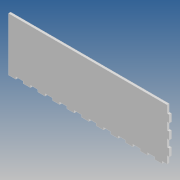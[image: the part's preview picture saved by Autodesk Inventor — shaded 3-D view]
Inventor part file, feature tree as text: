
AUTODESK INVENTOR PART (.ipt)
format: ipt  version: 2020 (Build 240168000, 168)  size: 154,112 bytes
history: native  units: mm
features: extrude x3, sketch x3, pattern_linear x2, other x1
ambient origin geometry x8: Origin, YZ Plane, XZ Plane, XY Plane, X Axis, Y Axis, Z Axis, Center Point
bodies: Body1 (feature_tree)
feature tree (9):
  other  "Твердое тело1"
  extrude  "Выдавливание1"  Depth=10.0mm
  pattern_linear  "Прямоуг.массив1"  Spacing1=3.0mm  [1 undecoded]
  extrude  "Выдавливание2"  Depth=3.0mm TaperAngle=0.0deg
  extrude  "Выдавливание3"  Depth=110.0mm
  pattern_linear  "Прямоуг.массив2"  Count1=7  [1 undecoded]
  sketch  "Эскиз1"
  sketch  "Эскиз2"
  sketch  "Эскиз3"
note: 2 required parameter values undecoded (feature->parameter linkage not recoverable at this tier; creation-order binding heuristic only, values carry confidence <= 0.55)
